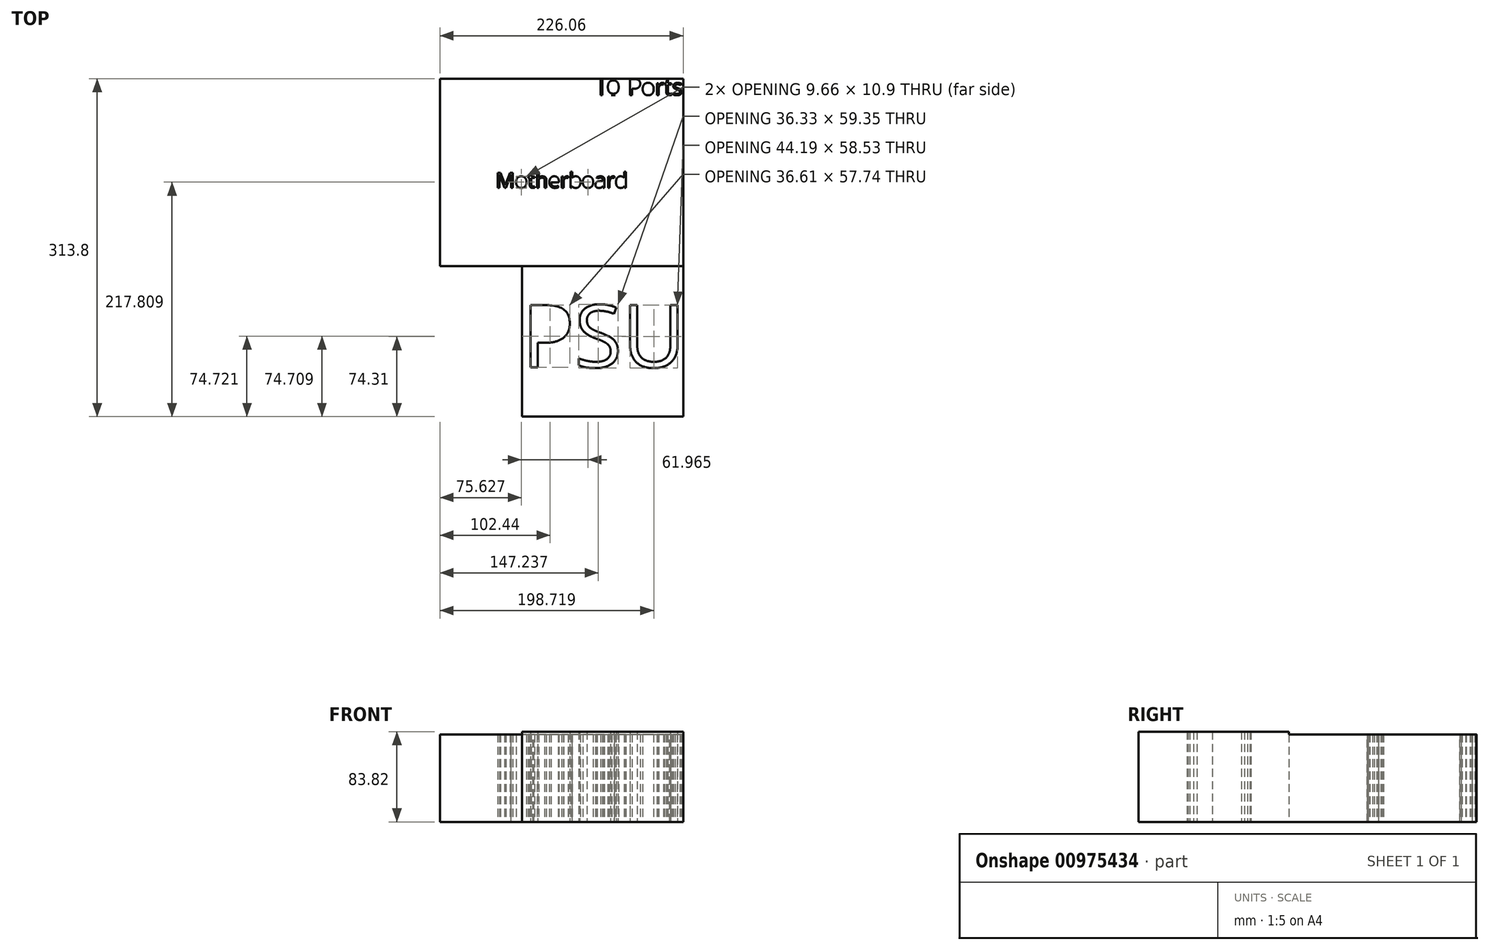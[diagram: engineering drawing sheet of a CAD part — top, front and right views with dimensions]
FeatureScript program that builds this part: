
annotation { "Feature Type Name" : "Feature", "Feature Type Description" : "" }
export const myFeature = defineFeature(function(context is Context, id is Id, definition is map)
    precondition{}
    {
        {
            var Q0;
            Q0=qCreatedBy(makeId("Top.planeOp"),FACE);
            var sketch = newSketch(context, id + "F0", { "sketchPlane" : qUnion([Q0])});
            skLineSegment(sketch, "E0.bottom", {"start": v(-113.03, 87) * mm, "end": v(113.03, 87) * mm});
            skLineSegment(sketch, "E0.top", {"start": v(-113.03, -87) * mm, "end": v(113.03, -87) * mm});
            skLineSegment(sketch, "E0.left", {"start": v(-113.03, 87) * mm, "end": v(-113.03, -87) * mm});
            skLineSegment(sketch, "E0.right", {"start": v(113.03, 87) * mm, "end": v(113.03, -87) * mm});
            skLineSegment(sketch, "E1.bottom", {"start": v(34.1, 87) * mm, "end": v(113.03, 87) * mm});
            skLineSegment(sketch, "E1.top", {"start": v(34.1, 71.96) * mm, "end": v(113.03, 71.96) * mm});
            skLineSegment(sketch, "E1.left", {"start": v(34.1, 87) * mm, "end": v(34.1, 71.96) * mm});
            skLineSegment(sketch, "E1.right", {"start": v(113.03, 87) * mm, "end": v(113.03, 71.96) * mm});
            skText(sketch, "E2", { "text": "Motherboard", "fontName": "OpenSans-Regular.ttf"});
            skText(sketch, "E3", { "text": "IO Ports", "fontName": "OpenSans-Regular.ttf"});
            skLineSegment(sketch, "E4", {"start": v(0, 87) * mm, "end": v(0, -87) * mm, "construction": true});
            const initialGuessF0  = {"E2": [-0.06108, -0.01415, 1, 0, 0.01415], "E3": [0.0341, 0.07196, 1, 0, 0.01503]};
            skSetInitialGuess(sketch, initialGuessF0);
            skSolve(sketch);
        }
        {
            var Q0;
            Q0=qCreatedBy(makeId("Top.planeOp"),FACE);
            var sketch = newSketch(context, id + "F1", { "sketchPlane" : qUnion([Q0])});
            skLineSegment(sketch, "E5.bottom", {"start": v(-36.83, -87) * mm, "end": v(113.03, -87) * mm});
            skLineSegment(sketch, "E5.top", {"start": v(-36.83, -226.7) * mm, "end": v(113.03, -226.7) * mm});
            skLineSegment(sketch, "E5.left", {"start": v(-36.83, -87) * mm, "end": v(-36.83, -226.7) * mm});
            skLineSegment(sketch, "E5.right", {"start": v(113.03, -87) * mm, "end": v(113.03, -226.7) * mm});
            skLineSegment(sketch, "E6.0", {"start": v(-113.03, -87) * mm, "end": v(113.03, -87) * mm});
            skLineSegment(sketch, "E7.0", {"start": v(113.03, 87) * mm, "end": v(113.03, -87) * mm});
            skText(sketch, "E8", { "text": "PSU", "fontName": "OpenSans-Regular.ttf"});
            const initialGuessF1  = {"E8": [-0.03683, -0.18086, 1, 0, 0.05823]};
            skSetInitialGuess(sketch, initialGuessF1);
            skSolve(sketch);
        }
        {
            var Q0;
            Q0=makeQuery(id+"F1.imprint","IMPRINT",FACE,{"disambiguationData":[TD([[makeQuery(id+"F1.imprint","IMPRINT",EDGE,{"derivedFrom":sQuery(id+"F1.wireOp",EDGE,"E5.top")}),1.0]])]});
            extrude(context, id + "F2", {"entities" : qUnion([Q0]), "depth" : 83.82 * mm, "offsetDistance" : 25.4 * mm});
        }
        {
            var Q0;
            Q0 = qSketchRegion(id + "F0", true);
            extrude(context, id + "F3", {"entities" : qUnion([Q0]), "operationType" : NewBodyOperationType.ADD, "depth" : 81.28 * mm, "offsetDistance" : 25.4 * mm});
        }
    });
